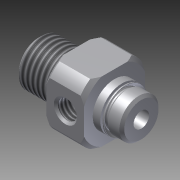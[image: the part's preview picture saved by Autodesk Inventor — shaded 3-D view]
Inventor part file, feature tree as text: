
AUTODESK INVENTOR PART (.ipt)
format: ipt  version: 2012 (Build 160160000, 160)  size: 233,472 bytes
history: native  units: in
note: dims shown in document units (in); Inventor stores cm internally (conversion verified against a paired STEP export)
features: other x91, sketch x7, revolve x4, hole x2, thread x1, extrude x1
ambient origin geometry x8: Origin, YZ Plane, XZ Plane, XY Plane, X Axis, Y Axis, Z Axis, Center Point
bodies: Solid1 (feature_tree)
feature tree (106):
  revolve  "Revolution1"  [1 undecoded]
  thread  "Thread1"  [1 undecoded]
  revolve  "Revolution2"  [1 undecoded]
  revolve  "Revolution3"  Angle=360.0deg
  hole  "Drilling 1"  [1 undecoded]
  extrude  "Extrusion1"  [1 undecoded]
  hole  "Drilling 2"  [1 undecoded]
  revolve  "Revolution4"  [1 undecoded]
  other  "sq1_XY"
  other  "sq1_YZ"
  other  "sq1_ZX"
  other  "sq1_X"
  other  "sq1_Y"
  other  "sq1_Z"
  other  "sq1_Center"
  other  "sq2_XY"
  other  "sq2_YZ"
  other  "sq2_ZX"
  other  "sq2_X"
  other  "sq2_Y"
  other  "sq2_Z"
  other  "sq2_Center"
  other  "rod_guide_XY"
  other  "rod_guide_YZ"
  other  "rod_guide_ZX"
  other  "rod_guide_X"
  other  "rod_guide_Y"
  other  "rod_guide_Z"
  other  "rod_guide_Center"
  other  "to_tube_XY"
  other  "to_tube_YZ"
  other  "to_tube_ZX"
  other  "to_tube_X"
  other  "to_tube_Y"
  other  "to_tube_Z"
  other  "to_tube_Center"
  other  "to_foot_bracket_XY"
  other  "to_foot_bracket_YZ"
  other  "to_foot_bracket_ZX"
  other  "to_foot_bracket_X"
  other  "to_foot_bracket_Y"
  other  "to_foot_bracket_Z"
  other  "to_foot_bracket_Center"
  other  "to_nut_XY"
  other  "to_nut_YZ"
  other  "to_nut_ZX"
  other  "to_nut_X"
  other  "to_nut_Y"
  other  "to_nut_Z"
  other  "to_nut_Center"
  other  "to_trunnion_brackets_XY"
  other  "to_trunnion_brackets_YZ"
  other  "to_trunnion_brackets_ZX"
  other  "to_trunnion_brackets_X"
  other  "to_trunnion_brackets_Y"
  other  "to_trunnion_brackets_Z"
  other  "to_trunnion_brackets_Center"
  other  "to_trunnion_brackets1_XY"
  other  "to_trunnion_brackets1_YZ"
  other  "to_trunnion_brackets1_ZX"
  other  "to_trunnion_brackets1_X"
  other  "to_trunnion_brackets1_Y"
  other  "to_trunnion_brackets1_Z"
  other  "to_trunnion_brackets1_Center"
  other  "to_trunnion_brackets2_XY"
  other  "to_trunnion_brackets2_YZ"
  other  "to_trunnion_brackets2_ZX"
  other  "to_trunnion_brackets2_X"
  other  "to_trunnion_brackets2_Y"
  other  "to_trunnion_brackets2_Z"
  other  "to_trunnion_brackets2_Center"
  other  "t111_XY"
  other  "t111_YZ"
  other  "t111_ZX"
  other  "t111_X"
  other  "t111_Y"
  other  "t111_Z"
  other  "t111_Center"
  other  "t1_XY"
  other  "t1_YZ"
  other  "t1_ZX"
  other  "t1_X"
  other  "t1_Y"
  other  "t1_Z"
  other  "t1_Center"
  other  "port_XY"
  other  "port_YZ"
  other  "port_ZX"
  other  "port_X"
  other  "port_Y"
  other  "port_Z"
  other  "port_Center"
  other  "to_screw_XY"
  other  "to_screw_YZ"
  other  "to_screw_ZX"
  other  "to_screw_X"
  other  "to_screw_Y"
  other  "to_screw_Z"
  other  "to_screw_Center"
  sketch  "Sketch_1"  dims[d0=360.0deg d1=0.2872in d2=0.0in d3=360.0deg]
  sketch  "Sketch_3"  dims[d4=360.0deg]
  sketch  "Sketch_17"
  sketch  "Sketch4"  dims[d5=0.128in d6=0.75in d7=0.158in d8=0.25in d9=90.0deg d10=0.845in d11=0.0in d12=0.845in d13=0.0in]
  sketch  "Sketch_16"
  sketch  "Sketch6"  dims[d14=0.156in d15=0.1735in d16=0.19in d17=0.25in d18=90.0deg d19=0.25in d20=0.0in d21=360.0deg]
  sketch  "Sketch_47"
note: 7 required parameter values undecoded (feature->parameter linkage not recoverable at this tier; creation-order binding heuristic only, values carry confidence <= 0.55)